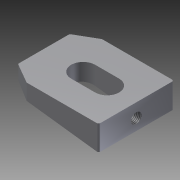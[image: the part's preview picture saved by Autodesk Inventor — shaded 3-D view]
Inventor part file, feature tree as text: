
AUTODESK INVENTOR PART (.ipt)
format: ipt  version: 2015 (Build 190159000, 159)  size: 158,208 bytes
history: native  units: mm (DEFAULTED — no unit token found)
features: sketch x5, extrude x4, hole x1, fillet x1
ambient origin geometry x8: Origin, YZ Plane, XZ Plane, XY Plane, X Axis, Y Axis, Z Axis, Center Point
bodies: Solid1 (feature_tree)
feature tree (11):
  extrude  "Extrusion4"  Depth=171.45mm
  extrude  "Extrusion5"  Depth=139.7mm
  extrude  "Extrusion6"  Depth=139.7mm TaperAngle=0.0deg
  extrude  "Extrusion7"  Depth=22.225mm
  hole  "Hole2"  [1 undecoded]
  fillet  "Fillet2"  Radius=139.7mm
  sketch  "Sketch5"  dims[d28=46.0375mm d29=171.45mm]
  sketch  "Sketch6"  dims[d30=139.7mm d31=0.0mm d32=304.8mm]
  sketch  "Sketch7"  dims[d33=38.1mm d34=139.7mm d35=0.0mm]
  sketch  "Sketch8"  dims[d36=69.85mm d37=22.225mm]
  sketch  "Sketch9"  dims[d38=73.025mm d39=44.45mm d40=139.7mm d41=0.0mm d42=30.0deg d43=38.1mm d44=139.7mm d45=0.0mm d46=69.85mm d47=25.4mm d48=19.177mm d49=12.7mm d50=9.525mm d51=6.35mm d52=14.3117mm d53=19.05mm d54=20.594885mm d55=3.175mm d56=30.0deg]
note: 1 required parameter value undecoded (feature->parameter linkage not recoverable at this tier; creation-order binding heuristic only, values carry confidence <= 0.55)
